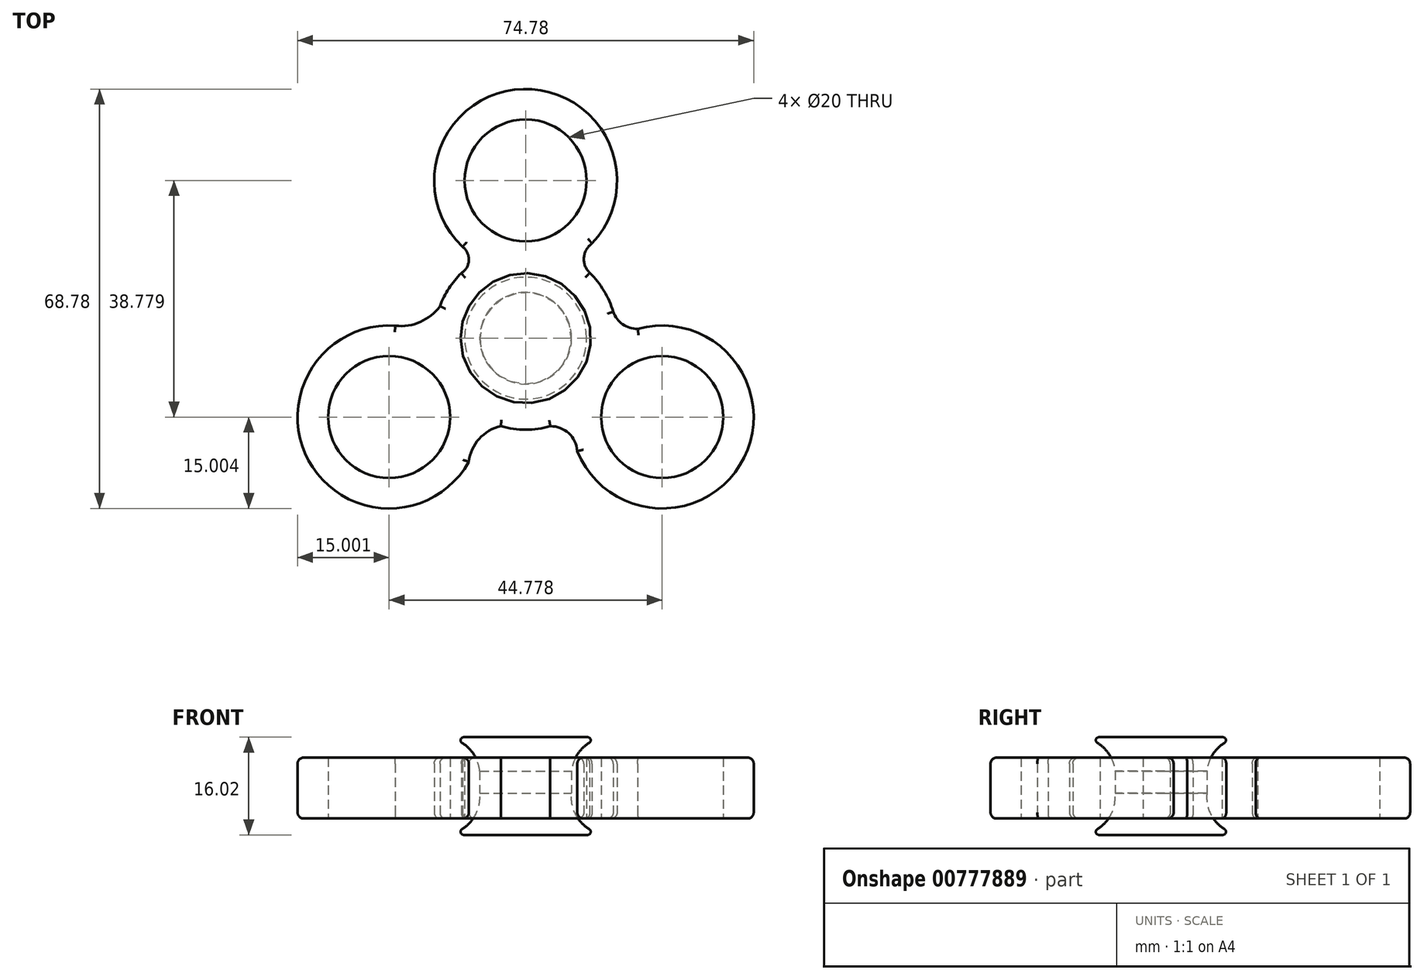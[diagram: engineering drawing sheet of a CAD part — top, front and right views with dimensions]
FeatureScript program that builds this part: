
annotation { "Feature Type Name" : "Feature", "Feature Type Description" : "" }
export const myFeature = defineFeature(function(context is Context, id is Id, definition is map)
    precondition{}
    {
        {
            var Q0;
            Q0=qCreatedBy(makeId("Top.planeOp"),FACE);
            var sketch = newSketch(context, id + "F0", { "sketchPlane" : qUnion([Q0])});
            skCircle(sketch, "E0", {"center": v(0, 0) * mm, "radius": 10 * mm});
            skCircle(sketch, "E1", {"center": v(0, 25.85) * mm, "radius": 10 * mm});
            skCircle(sketch, "E2", {"center": v(-22.39, -12.93) * mm, "radius": 10 * mm});
            skCircle(sketch, "E3", {"center": v(22.39, -12.93) * mm, "radius": 10 * mm});
            skArc(sketch, "E4.0", {"start": v(-20.92, 2) * mm, "mid": v(-35.7, -19.86) * mm, "end": v(-9.31, -20.27) * mm});
            skArc(sketch, "E5.0", {"start": v(10.13, 14.79) * mm, "mid": v(-0.1, 40.85) * mm, "end": v(-9.99, 14.66) * mm});
            skArc(sketch, "E6.0", {"start": v(7.82, -16.49) * mm, "mid": v(35.33, -20.5) * mm, "end": v(18.36, 1.52) * mm});
            skArc(sketch, "E7.0", {"start": v(-4.04, -14.45) * mm, "mid": v(0, -15) * mm, "end": v(4.04, -14.45) * mm});
            skArc(sketch, "E8", {"start": v(-21.36, 2.04) * mm, "mid": v(-17.26, 2.67) * mm, "end": v(-14.04, 5.27) * mm});
            skArc(sketch, "E9", {"start": v(-10.54, 10.67) * mm, "mid": v(-9.31, 12.77) * mm, "end": v(-10.34, 14.98) * mm});
            skArc(sketch, "E10", {"start": v(-4.04, -14.45) * mm, "mid": v(-7.63, -16.5) * mm, "end": v(-9.31, -20.27) * mm});
            skPoint(sketch, "E10.endSnap0", {"position": v(-9.31, 12.77) * mm});
            skArc(sketch, "E11", {"start": v(8.47, -18.52) * mm, "mid": v(7.07, -15.59) * mm, "end": v(4.04, -14.45) * mm});
            skArc(sketch, "E12", {"start": v(14.36, 4.33) * mm, "mid": v(15.91, 2.28) * mm, "end": v(18.36, 1.52) * mm});
            skArc(sketch, "E13", {"start": v(10.89, 15.53) * mm, "mid": v(9.55, 13.2) * mm, "end": v(10.51, 10.7) * mm});
            skArc(sketch, "E14.trimOffspring", {"start": v(-9.82, 11.34) * mm, "mid": v(-12.31, 8.57) * mm, "end": v(-14.04, 5.27) * mm});
            skArc(sketch, "E15.trimOffspring", {"start": v(14.36, 4.33) * mm, "mid": v(11.8, 9.26) * mm, "end": v(7.6, 12.93) * mm});
            skSolve(sketch);
        }
        {
            var Q0;
            Q0=makeQuery(id+"F0.imprint","IMPRINT",FACE,{"disambiguationData":[TD([[makeQuery(id+"F0.imprint","IMPRINT",EDGE,{"derivedFrom":sQuery(id+"F0.wireOp",EDGE,"E0")}),-1.0]])]});
            extrude(context, id + "F1", {"entities" : qUnion([Q0]), "depth" : 10 * mm, "offsetDistance" : 25 * mm});
        }
        {
            var Q0;
            Q0=makeQuery(id+"F1.opExtrude","CAP_EDGE",EDGE,{"disambiguationData":[OSD([sQuery(id+"F0.wireOp",EDGE,"E4.0")])],"isStart":false});
            var Q1;
            Q1=makeQuery(id+"F1.opExtrude","CAP_EDGE",EDGE,{"disambiguationData":[OSD([sQuery(id+"F0.wireOp",EDGE,"E8")])],"isStart":false});
            var Q2;
            Q2=makeQuery(id+"F1.opExtrude","CAP_EDGE",EDGE,{"disambiguationData":[OSD([sQuery(id+"F0.wireOp",EDGE,"E14.trimOffspring")])],"isStart":false});
            var Q3;
            Q3=makeQuery(id+"F1.opExtrude","CAP_EDGE",EDGE,{"disambiguationData":[OSD([sQuery(id+"F0.wireOp",EDGE,"E9")])],"isStart":false});
            var Q4;
            Q4=makeQuery(id+"F1.opExtrude","CAP_EDGE",EDGE,{"disambiguationData":[OSD([sQuery(id+"F0.wireOp",EDGE,"E5.0")])],"isStart":false});
            var Q5;
            Q5=makeQuery(id+"F1.opExtrude","CAP_EDGE",EDGE,{"disambiguationData":[OSD([sQuery(id+"F0.wireOp",EDGE,"E13")])],"isStart":false});
            var Q6;
            Q6=makeQuery(id+"F1.opExtrude","CAP_EDGE",EDGE,{"disambiguationData":[OSD([sQuery(id+"F0.wireOp",EDGE,"E15.trimOffspring")])],"isStart":false});
            var Q7;
            Q7=makeQuery(id+"F1.opExtrude","CAP_EDGE",EDGE,{"disambiguationData":[OSD([sQuery(id+"F0.wireOp",EDGE,"E12")])],"isStart":false});
            var Q8;
            Q8=makeQuery(id+"F1.opExtrude","CAP_EDGE",EDGE,{"disambiguationData":[OSD([sQuery(id+"F0.wireOp",EDGE,"E6.0")])],"isStart":false});
            var Q9;
            Q9=makeQuery(id+"F1.opExtrude","CAP_EDGE",EDGE,{"disambiguationData":[OSD([sQuery(id+"F0.wireOp",EDGE,"E11")])],"isStart":false});
            var Q10;
            Q10=makeQuery(id+"F1.opExtrude","CAP_EDGE",EDGE,{"disambiguationData":[OSD([sQuery(id+"F0.wireOp",EDGE,"E7.0")])],"isStart":false});
            var Q11;
            Q11=makeQuery(id+"F1.opExtrude","CAP_EDGE",EDGE,{"disambiguationData":[OSD([sQuery(id+"F0.wireOp",EDGE,"E10")])],"isStart":false});
            fillet(context, id + "F2", {"entities" : qUnion([Q0, Q1, Q2, Q3, Q4, Q5, Q6, Q7, Q8, Q9, Q10, Q11]), "radius" : 1 * mm, "tangentPropagation" : true, "allowEdgeOverflow" : false});
        }
        {
            var Q0;
            Q0=makeQuery(id+"F1.opExtrude","CAP_EDGE",EDGE,{"disambiguationData":[OSD([sQuery(id+"F0.wireOp",EDGE,"E4.0")])],"isStart":true});
            var Q1;
            Q1=makeQuery(id+"F1.opExtrude","CAP_EDGE",EDGE,{"disambiguationData":[OSD([sQuery(id+"F0.wireOp",EDGE,"E10")])],"isStart":true});
            var Q2;
            Q2=makeQuery(id+"F1.opExtrude","CAP_EDGE",EDGE,{"disambiguationData":[OSD([sQuery(id+"F0.wireOp",EDGE,"E7.0")])],"isStart":true});
            var Q3;
            Q3=makeQuery(id+"F1.opExtrude","CAP_EDGE",EDGE,{"disambiguationData":[OSD([sQuery(id+"F0.wireOp",EDGE,"E11")])],"isStart":true});
            var Q4;
            Q4=makeQuery(id+"F1.opExtrude","CAP_EDGE",EDGE,{"disambiguationData":[OSD([sQuery(id+"F0.wireOp",EDGE,"E6.0")])],"isStart":true});
            var Q5;
            Q5=makeQuery(id+"F1.opExtrude","CAP_EDGE",EDGE,{"disambiguationData":[OSD([sQuery(id+"F0.wireOp",EDGE,"E12")])],"isStart":true});
            var Q6;
            Q6=makeQuery(id+"F1.opExtrude","CAP_EDGE",EDGE,{"disambiguationData":[OSD([sQuery(id+"F0.wireOp",EDGE,"E15.trimOffspring")])],"isStart":true});
            var Q7;
            Q7=makeQuery(id+"F1.opExtrude","CAP_EDGE",EDGE,{"disambiguationData":[OSD([sQuery(id+"F0.wireOp",EDGE,"E13")])],"isStart":true});
            var Q8;
            Q8=makeQuery(id+"F1.opExtrude","CAP_EDGE",EDGE,{"disambiguationData":[OSD([sQuery(id+"F0.wireOp",EDGE,"E5.0")])],"isStart":true});
            var Q9;
            Q9=makeQuery(id+"F1.opExtrude","CAP_EDGE",EDGE,{"disambiguationData":[OSD([sQuery(id+"F0.wireOp",EDGE,"E9")])],"isStart":true});
            var Q10;
            Q10=makeQuery(id+"F1.opExtrude","CAP_EDGE",EDGE,{"disambiguationData":[OSD([sQuery(id+"F0.wireOp",EDGE,"E14.trimOffspring")])],"isStart":true});
            var Q11;
            Q11=makeQuery(id+"F1.opExtrude","CAP_EDGE",EDGE,{"disambiguationData":[OSD([sQuery(id+"F0.wireOp",EDGE,"E8")])],"isStart":true});
            fillet(context, id + "F3", {"entities" : qUnion([Q0, Q1, Q2, Q3, Q4, Q5, Q6, Q7, Q8, Q9, Q10, Q11]), "radius" : 1 * mm, "tangentPropagation" : true, "allowEdgeOverflow" : false});
        }
        {
            var Q0;
            Q0=qCreatedBy(makeId("Front.planeOp"),FACE);
            var sketch = newSketch(context, id + "F4", { "sketchPlane" : qUnion([Q0])});
            skLineSegment(sketch, "E16", {"start": v(0, 13.34) * mm, "end": v(0, -2.68) * mm});
            skLineSegment(sketch, "E17", {"start": v(0, -2.68) * mm, "end": v(-13.7, -2.68) * mm});
            skLineSegment(sketch, "E18", {"start": v(0, 13.34) * mm, "end": v(-13.7, 13.34) * mm});
            skArc(sketch, "E19", {"start": v(-7.53, 7.8) * mm, "mid": v(-9.55, 11.75) * mm, "end": v(-13.7, 13.34) * mm});
            skArc(sketch, "E20", {"start": v(-13.7, -2.68) * mm, "mid": v(-9.09, -0.63) * mm, "end": v(-7.53, 4.17) * mm});
            skLineSegment(sketch, "E21", {"start": v(-7.53, 7.8) * mm, "end": v(-7.53, 4.17) * mm});
            skSolve(sketch);
        }
        {
            var Q0;
            Q0=makeQuery(id+"F4.imprint","IMPRINT",FACE,{"disambiguationData":[TD([[makeQuery(id+"F4.imprint","IMPRINT",EDGE,{"derivedFrom":sQuery(id+"F4.wireOp",EDGE,"E16")}),-1.0]])]});
            var Q1;
            Q1=makeQuery(id+"F1.opExtrude","SWEPT_FACE",FACE,{"disambiguationData":[OSD([sQuery(id+"F0.wireOp",EDGE,"E0")])]});
            revolve(context, id + "F5", {"surfaceOperationType" : NewSurfaceOperationType.NEW, "entities" : qUnion([Q0]), "axis" : qUnion([Q1]), "revolveType" : RevolveType.FULL});
        }
        {
            var Q0;
            Q0=makeQuery(id+"F5.opRevolve","SWEPT_EDGE",EDGE,{"disambiguationData":[OSD([sQuery(id+"F4.wireOp",EDGE,"E18"),sQuery(id+"F4.wireOp",EDGE,"E19")])]});
            fillet(context, id + "F6", {"entities" : qUnion([Q0]), "radius" : 0.5 * mm, "tangentPropagation" : true, "allowEdgeOverflow" : false});
        }
        {
            var Q0;
            Q0=makeQuery(id+"F5.opRevolve","SWEPT_EDGE",EDGE,{"disambiguationData":[OSD([sQuery(id+"F4.wireOp",EDGE,"E17"),sQuery(id+"F4.wireOp",EDGE,"E20")])]});
            fillet(context, id + "F7", {"entities" : qUnion([Q0]), "radius" : 0.5 * mm, "tangentPropagation" : true, "allowEdgeOverflow" : false});
        }
    });
